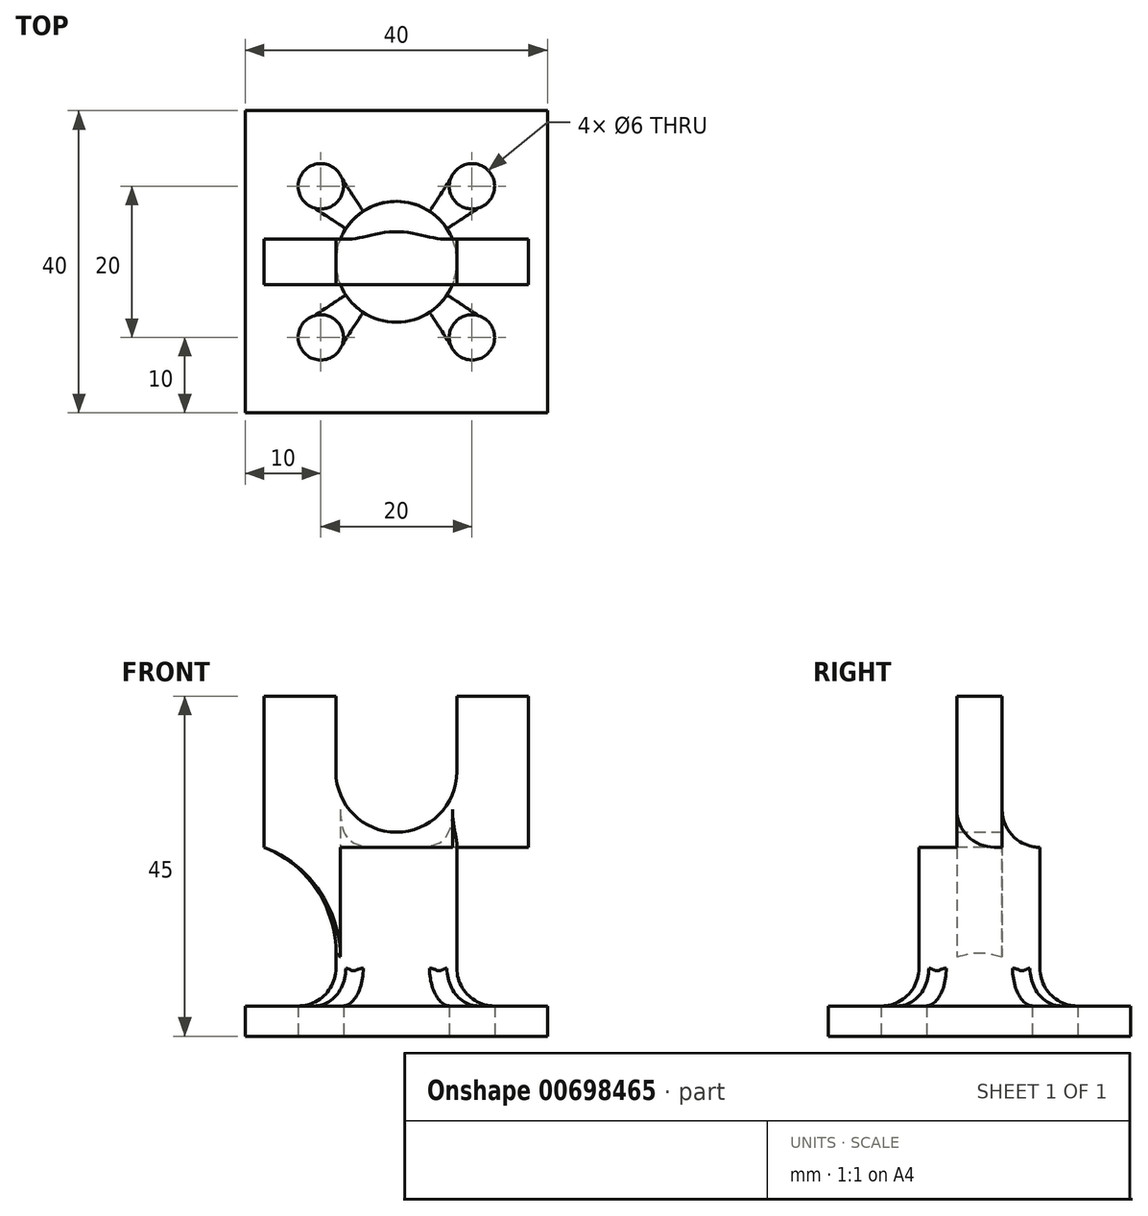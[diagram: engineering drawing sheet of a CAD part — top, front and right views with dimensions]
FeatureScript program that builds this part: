
annotation { "Feature Type Name" : "Feature", "Feature Type Description" : "" }
export const myFeature = defineFeature(function(context is Context, id is Id, definition is map)
    precondition{}
    {
        {
            var Q0;
            Q0=qCreatedBy(makeId("Top.planeOp"),FACE);
            var sketch = newSketch(context, id + "F0", { "sketchPlane" : qUnion([Q0])});
            skLineSegment(sketch, "E0.bottom", {"start": v(-20, 20) * mm, "end": v(20, 20) * mm});
            skLineSegment(sketch, "E0.top", {"start": v(-20, -20) * mm, "end": v(20, -20) * mm});
            skLineSegment(sketch, "E0.left", {"start": v(-20, 20) * mm, "end": v(-20, -20) * mm});
            skLineSegment(sketch, "E0.right", {"start": v(20, 20) * mm, "end": v(20, -20) * mm});
            skPoint(sketch, "E0.middle", {"position": v(0, 0) * mm});
            skLineSegment(sketch, "E1", {"start": v(0, 0) * mm, "end": v(-20, 20) * mm, "construction": true});
            skCircle(sketch, "E2", {"center": v(-10, 10) * mm, "radius": 3 * mm});
            skCircle(sketch, "E3.MirrorC", {"center": v(10, 10) * mm, "radius": 3 * mm});
            skCircle(sketch, "E4.MirrorC", {"center": v(10, -10) * mm, "radius": 3 * mm});
            skCircle(sketch, "E5.MirrorC", {"center": v(-10, -10) * mm, "radius": 3 * mm});
            skSolve(sketch);
        }
        {
            var Q0;
            Q0 = qSketchRegion(id + "F0", true);
            extrude(context, id + "F1", {"entities" : qUnion([Q0]), "depth" : 4 * mm, "offsetDistance" : 25 * mm});
        }
        {
            var Q0;
            Q0=qCreatedBy(makeId("Top.planeOp"),FACE);
            var sketch = newSketch(context, id + "F2", { "sketchPlane" : qUnion([Q0])});
            skCircle(sketch, "E6", {"center": v(0, 0) * mm, "radius": 8 * mm});
            skSolve(sketch);
        }
        {
            var Q0;
            Q0 = qSketchRegion(id + "F2", true);
            extrude(context, id + "F3", {"entities" : qUnion([Q0]), "operationType" : NewBodyOperationType.ADD, "depth" : 25 * mm, "offsetDistance" : 25 * mm});
        }
        {
            var Q0;
            Q0=makeQuery(id+"F3.opExtrude","CAP_FACE",FACE,{"disambiguationData":[OSD([sQuery(id+"F2.wireOp",EDGE,"E6")])],"isStart":false});
            var sketch = newSketch(context, id + "F4", { "sketchPlane" : qUnion([Q0])});
            skLineSegment(sketch, "E7.bottom", {"start": v(-17.5, 3) * mm, "end": v(17.5, 3) * mm});
            skLineSegment(sketch, "E7.top", {"start": v(-17.5, -3) * mm, "end": v(17.5, -3) * mm});
            skLineSegment(sketch, "E7.left", {"start": v(-17.5, 3) * mm, "end": v(-17.5, -3) * mm});
            skLineSegment(sketch, "E7.right", {"start": v(17.5, 3) * mm, "end": v(17.5, -3) * mm});
            skPoint(sketch, "E7.middle", {"position": v(0, 0) * mm});
            skSolve(sketch);
        }
        {
            var Q0;
            Q0 = qSketchRegion(id + "F4", true);
            extrude(context, id + "F5", {"entities" : qUnion([Q0]), "operationType" : NewBodyOperationType.ADD, "depth" : 20 * mm, "offsetDistance" : 25 * mm});
        }
        {
            var Q0;
            Q0=makeQuery(id+"F5.opExtrude","SWEPT_FACE",FACE,{"disambiguationData":[OSD([sQuery(id+"F4.wireOp",EDGE,"E7.bottom")])]});
            var sketch = newSketch(context, id + "F6", { "sketchPlane" : qUnion([Q0])});
            skLineSegment(sketch, "E8.0.0", {"start": v(7.42, 25) * mm, "end": v(17.5, 25) * mm, "construction": true});
            skLineSegment(sketch, "E8.0.1", {"start": v(17.5, 25) * mm, "end": v(17.5, 45) * mm, "construction": true});
            skLineSegment(sketch, "E8.0.2", {"start": v(17.5, 45) * mm, "end": v(-17.5, 45) * mm, "construction": true});
            skLineSegment(sketch, "E8.0.3", {"start": v(-17.5, 45) * mm, "end": v(-17.5, 25) * mm, "construction": true});
            skLineSegment(sketch, "E8.0.4", {"start": v(-17.5, 25) * mm, "end": v(-7.42, 25) * mm, "construction": true});
            skLineSegment(sketch, "E8.0.5", {"start": v(-7.42, 25) * mm, "end": v(7.42, 25) * mm, "construction": true});
            skPoint(sketch, "E9", {"position": v(0, 35) * mm});
            skPoint(sketch, "E9.positionSnap0", {"position": v(17.5, 35) * mm});
            skPoint(sketch, "E9.positionSnap1", {"position": v(0, 45) * mm});
            skArc(sketch, "E10", {"start": v(-8, 35) * mm, "mid": v(0, 27) * mm, "end": v(8, 35) * mm});
            skLineSegment(sketch, "E11", {"start": v(-8, 35) * mm, "end": v(-8, 45) * mm});
            skLineSegment(sketch, "E12", {"start": v(8, 35) * mm, "end": v(8, 45) * mm});
            skLineSegment(sketch, "E13", {"start": v(8, 45) * mm, "end": v(-8, 45) * mm});
            skSolve(sketch);
        }
        {
            var Q0;
            Q0=makeQuery(id+"F6.imprint","IMPRINT",FACE,{"disambiguationData":[TD([[makeQuery(id+"F6.imprint","IMPRINT",EDGE,{"derivedFrom":sQuery(id+"F6.wireOp",EDGE,"E10")}),1.0]])]});
            extrude(context, id + "F7", {"entities" : qUnion([Q0]), "operationType" : NewBodyOperationType.REMOVE, "oppositeDirection" : true, "depth" : 10 * mm, "offsetDistance" : 25 * mm});
        }
        {
            var Q0;
            {var subQ0=sQuery(id+"F2.wireOp",EDGE,"E6");Q0=makeQuery(id+"F5.boolean.opBoolean","SPLIT",EDGE,{"disambiguationData":[topologyDisambiguationEdgeConnected([makeQuery(id+"F3.opExtrude","SWEPT_FACE",FACE,{"disambiguationData":[OSD([subQ0])]}),makeQuery(id+"F5.opExtrude","CAP_FACE",FACE,{"disambiguationData":[OSD([sQuery(id+"F4.wireOp",EDGE,"E7.bottom"),sQuery(id+"F4.wireOp",EDGE,"E7.top"),sQuery(id+"F4.wireOp",EDGE,"E7.left"),sQuery(id+"F4.wireOp",EDGE,"E7.right")])],"isStart":true})]),OD(0.0)],"derivedFrom":makeQuery(id+"F3.opExtrude","CAP_EDGE",EDGE,{"disambiguationData":[OSD([subQ0])],"isStart":false})});}
            var Q1;
            {var subQ0=sQuery(id+"F2.wireOp",EDGE,"E6");Q1=makeQuery(id+"F5.boolean.opBoolean","SPLIT",EDGE,{"disambiguationData":[topologyDisambiguationEdgeConnected([makeQuery(id+"F3.opExtrude","SWEPT_FACE",FACE,{"disambiguationData":[OSD([subQ0])]}),makeQuery(id+"F5.opExtrude","CAP_FACE",FACE,{"disambiguationData":[OSD([sQuery(id+"F4.wireOp",EDGE,"E7.bottom"),sQuery(id+"F4.wireOp",EDGE,"E7.top"),sQuery(id+"F4.wireOp",EDGE,"E7.left"),sQuery(id+"F4.wireOp",EDGE,"E7.right")])],"isStart":true})]),OD(1.0)],"derivedFrom":makeQuery(id+"F3.opExtrude","CAP_EDGE",EDGE,{"disambiguationData":[OSD([subQ0])],"isStart":false})});}
            fillet(context, id + "F8", {"entities" : qUnion([Q0, Q1]), "radius" : 15 * mm, "tangentPropagation" : true, "allowEdgeOverflow" : false});
        }
        {
            var Q0;
            {var subQ0=sQuery(id+"F4.wireOp",EDGE,"E7.top");Q0=makeQuery(id+"F5.boolean.opBoolean","SPLIT",EDGE,{"disambiguationData":[topologyDisambiguationEdgeConnected([makeQuery(id+"F3.opExtrude","CAP_FACE",FACE,{"disambiguationData":[OSD([sQuery(id+"F2.wireOp",EDGE,"E6")])],"isStart":false}),makeQuery(id+"F5.opExtrude","SWEPT_FACE",FACE,{"disambiguationData":[OSD([subQ0])]})])],"derivedFrom":makeQuery(id+"F5.opExtrude","CAP_EDGE",EDGE,{"disambiguationData":[OSD([subQ0])],"isStart":true})});}
            var Q1;
            {var subQ0=sQuery(id+"F4.wireOp",EDGE,"E7.bottom");Q1=makeQuery(id+"F5.boolean.opBoolean","SPLIT",EDGE,{"disambiguationData":[topologyDisambiguationEdgeConnected([makeQuery(id+"F3.opExtrude","CAP_FACE",FACE,{"disambiguationData":[OSD([sQuery(id+"F2.wireOp",EDGE,"E6")])],"isStart":false}),makeQuery(id+"F5.opExtrude","SWEPT_FACE",FACE,{"disambiguationData":[OSD([subQ0])]})])],"derivedFrom":makeQuery(id+"F5.opExtrude","CAP_EDGE",EDGE,{"disambiguationData":[OSD([subQ0])],"isStart":true})});}
            fillet(context, id + "F9", {"entities" : qUnion([Q0, Q1]), "radius" : 5 * mm, "tangentPropagation" : true, "allowEdgeOverflow" : false});
        }
        {
            var Q0;
            Q0=makeQuery(id+"F3.boolean.opBoolean","INTERSECT",EDGE,{"derivedFrom":[makeQuery(id+"F1.opExtrude","CAP_FACE",FACE,{"disambiguationData":[OSD([sQuery(id+"F0.wireOp",EDGE,"E0.bottom"),sQuery(id+"F0.wireOp",EDGE,"E0.top"),sQuery(id+"F0.wireOp",EDGE,"E0.left"),sQuery(id+"F0.wireOp",EDGE,"E0.right"),sQuery(id+"F0.wireOp",EDGE,"E2"),sQuery(id+"F0.wireOp",EDGE,"E3.MirrorC"),sQuery(id+"F0.wireOp",EDGE,"E4.MirrorC"),sQuery(id+"F0.wireOp",EDGE,"E5.MirrorC")])],"isStart":false}),makeQuery(id+"F3.opExtrude","SWEPT_FACE",FACE,{"disambiguationData":[OSD([sQuery(id+"F2.wireOp",EDGE,"E6")])]})]});
            fillet(context, id + "F10", {"entities" : qUnion([Q0]), "radius" : 5 * mm, "tangentPropagation" : true, "allowEdgeOverflow" : false});
        }
    });
